# Revit family: Furniture-Console_Table_Legs-KOHLER-Memoirs-K-30010
name_source: partatom
category: Specialty Equipment
revit_build: Autodesk Revit 2015 (Build: 20140606_1530(x64)
units: mm (PartAtom-declared; Revit-internal decimal feet)

## types (4) — shared parameters
ADA Compliant = No
Assembly Code = C1030200
Date Modified = 12/11/2018
Default Elevation = 42"
Description = Console table legs for K-2259 Memoirs sink
Height = 32 1/4"
Length = 19 7/8"
Manufacturer = KOHLER Co.
MasterFormat 1995 = 10820
MasterFormat 2004 = 10.28.13
Material = Solid Brass
Product Documentation Link = http://www.us.kohler.com
Product Name = Memoirs
Product Page URL = http://www.us.kohler.com
URL = https://www.us.kohler.com
Width = 22 15/16"

## per-type parameters (varying)
| type | Finish | Model | Type |
| CP-Polished Chrome | Kohler-Metal-CP-Polished_Chrome | K-30010-CP | 1 |
| BN-Vibrant Brushed Nickel | Kohler-Metal-BN-Vibrant_Brushed_Nickel | K-30010-BN | 2 |
| BV-Vibrant Brushed Bronze | Kohler-Metal-BV-Brushed_Bronze | K-30010-BV | 3 |
| 2BZ-Oil_Rubbed Bronze | Kohler-Metal-2BZ-Oil_Rubbed_Bronze | K-30010-2BZ | 4 |

## geometry (parser evidence)
native form markers: Sweep x5
no freeform markers — native parametric forms only
